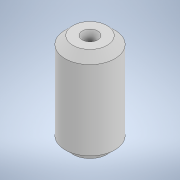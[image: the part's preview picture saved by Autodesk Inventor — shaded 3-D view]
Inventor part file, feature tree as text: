
AUTODESK INVENTOR PART (.ipt)
format: ipt  version: 2020 (Build 240168000, 168)  size: 109,056 bytes
history: native  units: in
note: dims shown in document units (in); Inventor stores cm internally (conversion verified against a paired STEP export)
features: revolve x1, sketch x1
ambient origin geometry x8: Origin, YZ Plane, XZ Plane, XY Plane, X Axis, Y Axis, Z Axis, Center Point
bodies: Solid1 (feature_tree)
feature tree (2):
  revolve  "Revolution1"  [1 undecoded]
  sketch  "Sketch1"  dims[d0=0.25in d1=0.11in d2=0.078in d3=135.0deg d4=0.952in d5=90.0deg]
note: 1 required parameter value undecoded (feature->parameter linkage not recoverable at this tier; creation-order binding heuristic only, values carry confidence <= 0.55)
